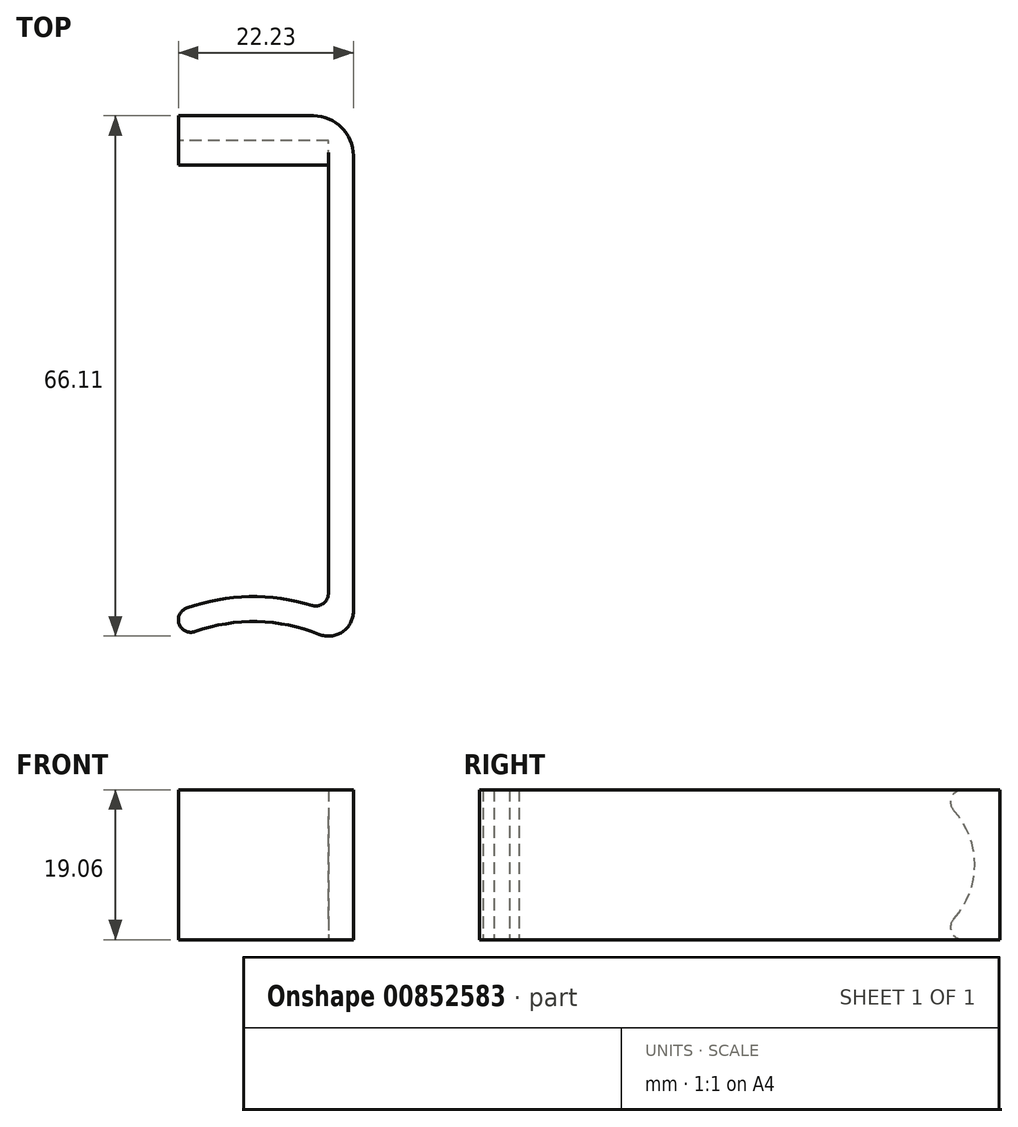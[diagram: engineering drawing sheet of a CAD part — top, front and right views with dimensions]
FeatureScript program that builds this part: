
annotation { "Feature Type Name" : "Feature", "Feature Type Description" : "" }
export const myFeature = defineFeature(function(context is Context, id is Id, definition is map)
    precondition{}
    {
        {
            var Q0;
            Q0=qCreatedBy(makeId("Top.planeOp"),FACE);
            var sketch = newSketch(context, id + "F0", { "sketchPlane" : qUnion([Q0])});
            skLineSegment(sketch, "E0", {"start": v(0, 0) * mm, "end": v(19.05, 0) * mm});
            skLineSegment(sketch, "E1", {"start": v(19.05, 0) * mm, "end": v(19.05, -57.52) * mm});
            skArc(sketch, "E2", {"start": v(17, -59.04) * mm, "mid": v(9, -57.92) * mm, "end": v(1.06, -59.36) * mm});
            skLineSegment(sketch, "E3", {"start": v(0, 0) * mm, "end": v(0, -59.77) * mm, "construction": true});
            skPoint(sketch, "E4", {"position": v(9.53, -57.91) * mm});
            skArc(sketch, "E5.0", {"start": v(17.86, -62.7) * mm, "mid": v(10.02, -61.1) * mm, "end": v(2.12, -62.36) * mm});
            skLineSegment(sketch, "E5.1", {"start": v(22.23, 3.17) * mm, "end": v(22.22, -59.77) * mm});
            skLineSegment(sketch, "E5.2", {"start": v(0, 3.17) * mm, "end": v(22.22, 3.17) * mm});
            skLineSegment(sketch, "E6", {"start": v(0, 3.17) * mm, "end": v(0, 0) * mm});
            skLineSegment(sketch, "E7", {"start": v(0, -60.86) * mm, "end": v(0, -60.86) * mm});
            skPoint(sketch, "E8.visualSharp", {"position": v(22.22, -65.07) * mm});
            skArc(sketch, "E8.filletArc", {"start": v(17.86, -62.7) * mm, "mid": v(20.82, -62.4) * mm, "end": v(22.22, -59.77) * mm});
            skArc(sketch, "E9.filletArc", {"start": v(17, -59.04) * mm, "mid": v(18.4, -58.8) * mm, "end": v(19.05, -57.52) * mm});
            skPoint(sketch, "E10.visualSharp", {"position": v(0, -59.77) * mm});
            skArc(sketch, "E10.filletArc", {"start": v(1.06, -59.36) * mm, "mid": v(0.3, -59.94) * mm, "end": v(0, -60.86) * mm});
            skPoint(sketch, "E11.visualSharp", {"position": v(0, -63.23) * mm});
            skArc(sketch, "E11.filletArc", {"start": v(0, -60.86) * mm, "mid": v(0.67, -62.16) * mm, "end": v(2.12, -62.36) * mm});
            skSolve(sketch);
        }
        {
            var Q0;
            Q0=qCreatedBy(makeId("Right.planeOp"),FACE);
            var sketch = newSketch(context, id + "F1", { "sketchPlane" : qUnion([Q0])});
            skLineSegment(sketch, "E12", {"start": v(0, -9.53) * mm, "end": v(0, 9.53) * mm});
            skLineSegment(sketch, "E13", {"start": v(0, -9.53) * mm, "end": v(-6.62, -9.53) * mm});
            skLineSegment(sketch, "E14", {"start": v(0, 9.53) * mm, "end": v(-6.62, 9.53) * mm});
            skArc(sketch, "E15", {"start": v(-6.62, -9.53) * mm, "mid": v(0, 0) * mm, "end": v(-6.62, 9.53) * mm});
            skSolve(sketch);
        }
        {
            var Q0;
            Q0=makeQuery(id+"F0.imprint","IMPRINT",FACE,{"disambiguationData":[TD([[makeQuery(id+"F0.imprint","IMPRINT",EDGE,{"derivedFrom":sQuery(id+"F0.wireOp",EDGE,"E0")}),1.0]])]});
            extrude(context, id + "F2", {"entities" : qUnion([Q0]), "endBound" : BoundingType.SYMMETRIC, "depth" : 19.05 * mm, "offsetDistance" : 25.4 * mm});
        }
        {
            var Q0;
            {var subQ0=sQuery(id+"F1.wireOp",EDGE,"E13");Q0=makeQuery(id+"F1.imprint","IMPRINT",FACE,{"disambiguationData":[TD([[makeQuery(id+"F1.imprint","IMPRINT",EDGE,{"derivedFrom":subQ0}),-1.0]])]});}
            var Q1;
            {var subQ0=sQuery(id+"F1.wireOp",EDGE,"E14");Q1=makeQuery(id+"F1.imprint","IMPRINT",FACE,{"disambiguationData":[TD([[makeQuery(id+"F1.imprint","IMPRINT",EDGE,{"derivedFrom":subQ0}),1.0]])]});}
            var Q2;
            Q2=makeQuery(id+"F2.opExtrude","SWEPT_FACE",FACE,{"disambiguationData":[OSD([sQuery(id+"F0.wireOp",EDGE,"E1")])]});
            extrude(context, id + "F3", {"entities" : qUnion([Q0, Q1]), "operationType" : NewBodyOperationType.ADD, "endBound" : BoundingType.UP_TO_SURFACE, "depth" : 25.4 * mm, "endBoundEntityFace" : qUnion([Q2]), "offsetDistance" : 25.4 * mm});
        }
        {
            var Q0;
            Q0=makeQuery(id+"F3.opExtrude","SWEPT_EDGE",EDGE,{"disambiguationData":[OSD([sQuery(id+"F1.wireOp",EDGE,"E14"),sQuery(id+"F1.wireOp",EDGE,"E15")])]});
            var Q1;
            Q1=makeQuery(id+"F3.opExtrude","SWEPT_EDGE",EDGE,{"disambiguationData":[OSD([sQuery(id+"F1.wireOp",EDGE,"E13"),sQuery(id+"F1.wireOp",EDGE,"E15")])]});
            fillet(context, id + "F4", {"entities" : qUnion([Q0, Q1]), "radius" : 1.59 * mm, "tangentPropagation" : true, "allowEdgeOverflow" : false});
        }
        {
            var Q0;
            Q0=makeQuery(id+"F2.opExtrude","SWEPT_EDGE",EDGE,{"disambiguationData":[OSD([sQuery(id+"F0.wireOp",EDGE,"E5.1"),sQuery(id+"F0.wireOp",EDGE,"E5.2")])]});
            fillet(context, id + "F5", {"entities" : qUnion([Q0]), "radius" : 5.08 * mm, "tangentPropagation" : true, "allowEdgeOverflow" : false});
        }
    });
